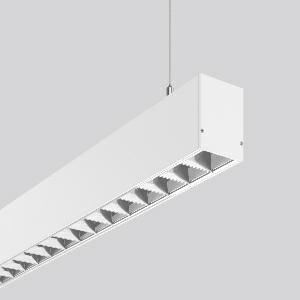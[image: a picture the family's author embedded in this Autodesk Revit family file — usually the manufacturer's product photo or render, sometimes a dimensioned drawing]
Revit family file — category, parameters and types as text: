
# Revit family: less_is_more_50_312337_002_1_76_124e
name_source: partatom
category: Lighting Fixtures
units: mm (PartAtom-declared; Revit-internal decimal feet)

## family parameters
Cut with Voids When Loaded = No
Host = Face
Light Source = No
Part Type = Normal
Room Calculation Point = No
Round Connector Dimension = Use Diameter
Shared = No

## types (1)
- LESS IS MORE 50 (1 x LED Modul 840, 4450 lm, 4000)
    Apparent Load = 35 VA
    CIE Flux Codes = 95 100 100 100 100
    Color Rendering = 80
    Color Temperature = 4000
    Default Elevation = 1800 mm
    Description = Series: LESS IS MORE 50
Linear pendant luminaire for aesthetically sophisticated lighting. Housing: extruded aluminium profile, powder-coated. End cap aluminium powder-coated. Canopy made of aluminium, powder-coated. Alea optical system: Reflector structure (ABS, Aluminium-coated, highly polished) with integrated diffuser made of non-yellowing plastic (PMMA) opal for glare-free light at the workstation (screen-compliant according to EN 12464-1). Direct light emission. Suitable for pendant. 2-point steel cable suspension freely positionable and infinitely height-adjustable. Special lengths available on request. LED unit with integrated converter interchangeable and removable. Suitable for through-wiring. With sensors or as a safety luminaire on request. 
Colour: traffic white, matt (RAL 9016)
Length: 1407 mm
Width: 57 mm
Height: 75 mm
Suspension length: 2000 mm
Lamp: LED
Socket: without socket
Colour temperature: 4000K
Colour rendering index (CRI): 80
System power: 35 W
Rated luminous flux: 4450 lm
Luminous efficiency: 127 lm/W
Control gear: Converter, dimmable, DALI
Protection class: I
Type of protection: IP 20
    Height = 75 mm
    Lamp = 1 x LED Modul 840
    Lamp Light Flux = 4450 lm
    Lamp count = 1
    Length = 1407 mm
    Lifetime = 50000 h
    Luminous efficacy = 127 lm/W
    Manufacturer = RZB
    ModVariant = No
    Model = 312337.002.1.76
    Mounting Place = Ceiling
    Mounting Type = Pendant
    Number of Poles = 1
    OnlyDefault = Yes
    Power Factor = 1
    Product Name = LESS IS MORE 50
    Product group = Pendant LED linear luminaires
    ProductGroupID = 907
    Protection Class = Protection class I
    Protection Degree = IP 20
    RLX_Detail_Level = 1
    RLX_Emergency_Light_Flux = 0 lm
    RLX_Emergency_Type = 0
    RLX_Emergency_Type_DB = No
    RlxData = <blob elided: 33165 chars, md5=79deb5d6>
    Socket = socket
    Standby Power = 0 W
    System Light Flux = 4450 lm
    System Power = 35 W
    Type Comments = Product without accessories
    Type Image = 312342.002.jpg
    URL = http://relux.com
    VarID = ---
    Voltage = 230 V
    Voltage Range = 220-240 V
    Weight = 0.00 kg
    Width = 57 mm

## geometry (parser evidence)
native form markers: Blend x4, Sweep x10
no freeform markers — native parametric forms only
